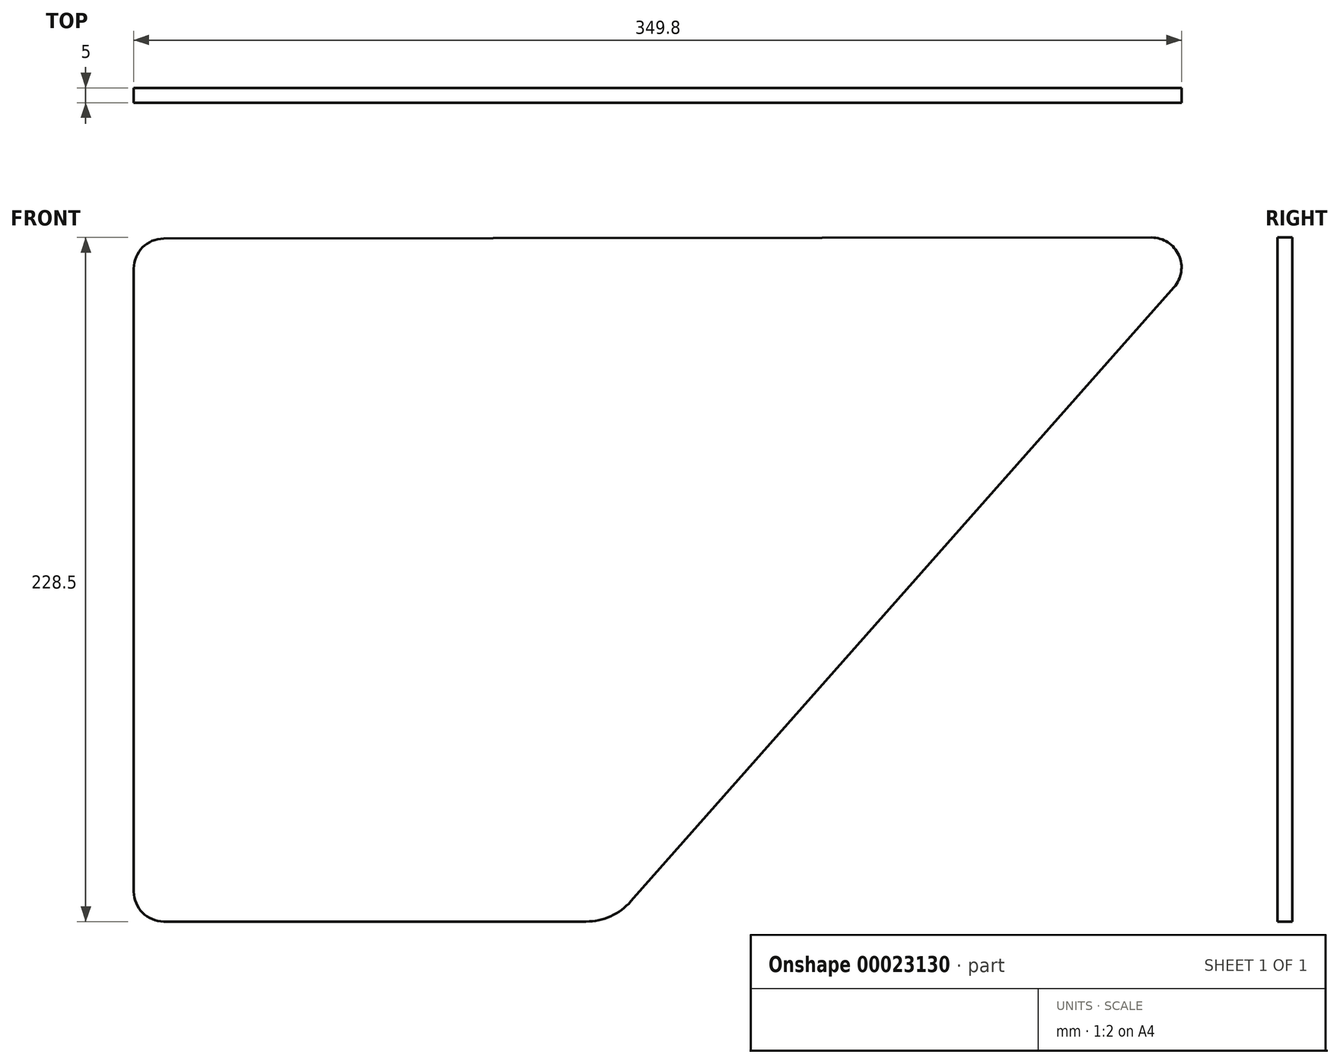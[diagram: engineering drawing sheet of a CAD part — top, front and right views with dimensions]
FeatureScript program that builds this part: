
annotation { "Feature Type Name" : "Feature", "Feature Type Description" : "" }
export const myFeature = defineFeature(function(context is Context, id is Id, definition is map)
    precondition{}
    {
        {
            var Q0;
            Q0=qCreatedBy(makeId("Front.planeOp"),FACE);
            var sketch = newSketch(context, id + "F0", { "sketchPlane" : qUnion([Q0])});
            skLineSegment(sketch, "E0", {"start": v(-147.98, 93.1) * mm, "end": v(181.81, 93.47) * mm});
            skLineSegment(sketch, "E1", {"start": v(189.32, 76.85) * mm, "end": v(8, -128.27) * mm});
            skLineSegment(sketch, "E2", {"start": v(-6.98, -135.03) * mm, "end": v(-147.97, -135.03) * mm});
            skLineSegment(sketch, "E3", {"start": v(-157.97, -125.03) * mm, "end": v(-157.97, 83.1) * mm});
            skPoint(sketch, "E4.visualSharp", {"position": v(-157.97, 93.09) * mm});
            skArc(sketch, "E4.filletArc", {"start": v(-147.98, 93.1) * mm, "mid": v(-155.04, 90.17) * mm, "end": v(-157.97, 83.1) * mm});
            skPoint(sketch, "E5.visualSharp", {"position": v(-157.97, -135.03) * mm});
            skArc(sketch, "E5.filletArc", {"start": v(-157.97, -125.03) * mm, "mid": v(-155.04, -132.1) * mm, "end": v(-147.97, -135.03) * mm});
            skPoint(sketch, "E6.visualSharp", {"position": v(204.03, 93.5) * mm});
            skArc(sketch, "E6.filletArc", {"start": v(189.32, 76.85) * mm, "mid": v(190.94, 87.58) * mm, "end": v(181.81, 93.47) * mm});
            skPoint(sketch, "E7.visualSharp", {"position": v(2.03, -135.03) * mm});
            skArc(sketch, "E7.filletArc", {"start": v(-6.98, -135.03) * mm, "mid": v(1.24, -133.26) * mm, "end": v(8, -128.27) * mm});
            skLineSegment(sketch, "E8.bottom", {"start": v(-157.97, 93.09) * mm, "end": v(204.03, 93.09) * mm, "construction": true});
            skLineSegment(sketch, "E8.top", {"start": v(-157.97, -135.03) * mm, "end": v(204.03, -135.03) * mm, "construction": true});
            skLineSegment(sketch, "E8.left", {"start": v(-157.97, 93.09) * mm, "end": v(-157.97, -135.03) * mm, "construction": true});
            skLineSegment(sketch, "E8.right", {"start": v(204.03, 93.09) * mm, "end": v(204.03, -135.03) * mm, "construction": true});
            skLineSegment(sketch, "E9", {"start": v(191.83, 111.91) * mm, "end": v(191.83, -158.25) * mm, "construction": true});
            skSolve(sketch);
        }
        {
            var Q0;
            Q0 = qSketchRegion(id + "F0", true);
            extrude(context, id + "F1", {"entities" : qUnion([Q0]), "depth" : 5 * mm});
        }
    });
